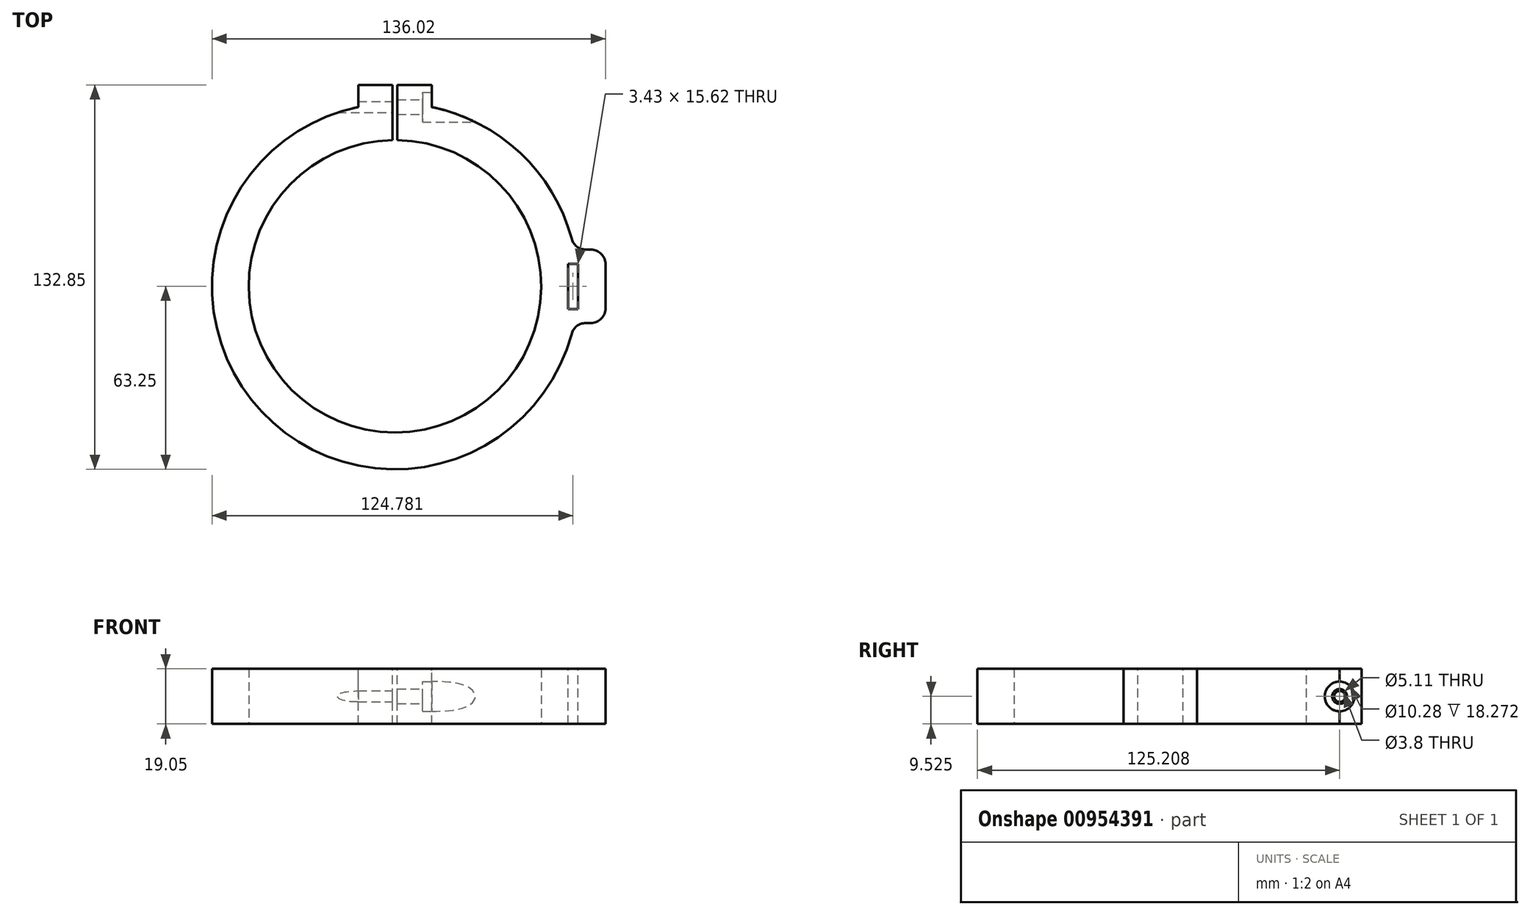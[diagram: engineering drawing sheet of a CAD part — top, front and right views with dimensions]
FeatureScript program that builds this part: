
annotation { "Feature Type Name" : "Feature", "Feature Type Description" : "" }
export const myFeature = defineFeature(function(context is Context, id is Id, definition is map)
    precondition{}
    {
        {
            var Q0;
            Q0=qCreatedBy(makeId("Top.planeOp"),FACE);
            var sketch = newSketch(context, id + "F0", { "sketchPlane" : qUnion([Q0])});
            skCircle(sketch, "E0", {"center": v(0, 0) * mm, "radius": 50.55 * mm});
            skCircle(sketch, "E1", {"center": v(0, 0) * mm, "radius": 63.25 * mm});
            skSolve(sketch);
        }
        {
            var Q0;
            Q0=makeQuery(id+"F0.imprint","IMPRINT",FACE,{"disambiguationData":[TD([[makeQuery(id+"F0.imprint","IMPRINT",EDGE,{"derivedFrom":sQuery(id+"F0.wireOp",EDGE,"E0")}),-1.0]])]});
            extrude(context, id + "F1", {"entities" : qUnion([Q0]), "depth" : 19.05 * mm, "offsetDistance" : 25.4 * mm});
        }
        {
            var Q0;
            Q0=makeQuery(id+"F1.opExtrude","CAP_FACE",FACE,{"disambiguationData":[OSD([sQuery(id+"F0.wireOp",EDGE,"E0"),sQuery(id+"F0.wireOp",EDGE,"E1")])],"isStart":false});
            var sketch = newSketch(context, id + "F2", { "sketchPlane" : qUnion([Q0])});
            skLineSegment(sketch, "E2.bottom", {"start": v(-12.7, 69.6) * mm, "end": v(12.7, 69.6) * mm});
            skLineSegment(sketch, "E2.top", {"start": v(-12.7, 50.55) * mm, "end": v(12.7, 50.55) * mm});
            skLineSegment(sketch, "E2.left", {"start": v(-12.7, 69.6) * mm, "end": v(-12.7, 50.55) * mm});
            skLineSegment(sketch, "E2.right", {"start": v(12.7, 69.6) * mm, "end": v(12.7, 50.55) * mm});
            skSolve(sketch);
        }
        {
            var Q0;
            {var subQ0=sQuery(id+"F2.wireOp",EDGE,"E2.bottom");Q0=makeQuery(id+"F2.imprint","IMPRINT",FACE,{"disambiguationData":[TD([[makeQuery(id+"F2.imprint","IMPRINT",EDGE,{"derivedFrom":subQ0}),-1.0]])]});}
            extrude(context, id + "F3", {"entities" : qUnion([Q0]), "operationType" : NewBodyOperationType.ADD, "oppositeDirection" : true, "depth" : 19.05 * mm, "offsetDistance" : 25.4 * mm});
        }
        {
            var Q0;
            {var subQ0=sQuery(id+"F0.wireOp",EDGE,"E1");Q0=makeQuery(id+"F3.boolean.opBoolean","MERGE",FACE,{"derivedFrom":[makeQuery(id+"F1.opExtrude","CAP_FACE",FACE,{"disambiguationData":[OSD([sQuery(id+"F0.wireOp",EDGE,"E0"),subQ0])],"isStart":false}),makeQuery(id+"F3.opExtrude","CAP_FACE",FACE,{"disambiguationData":[OSD([subQ0,sQuery(id+"F2.wireOp",EDGE,"E2.bottom"),sQuery(id+"F2.wireOp",EDGE,"E2.left"),sQuery(id+"F2.wireOp",EDGE,"E2.right")])],"isStart":true})]});}
            var sketch = newSketch(context, id + "F4", { "sketchPlane" : qUnion([Q0])});
            skLineSegment(sketch, "E3.bottom", {"start": v(-0.8, 69.6) * mm, "end": v(0.8, 69.6) * mm});
            skLineSegment(sketch, "E3.top", {"start": v(-0.8, 50.54) * mm, "end": v(0.8, 50.54) * mm});
            skLineSegment(sketch, "E3.left", {"start": v(-0.8, 69.6) * mm, "end": v(-0.8, 50.54) * mm});
            skLineSegment(sketch, "E3.right", {"start": v(0.8, 69.6) * mm, "end": v(0.8, 50.54) * mm});
            skSolve(sketch);
        }
        {
            var Q0;
            Q0 = qSketchRegion(id + "F4", true);
            extrude(context, id + "F5", {"entities" : qUnion([Q0]), "operationType" : NewBodyOperationType.REMOVE, "endBound" : BoundingType.THROUGH_ALL, "oppositeDirection" : true, "depth" : 25.4 * mm, "offsetDistance" : 25.4 * mm});
        }
        {
            var Q0;
            Q0=makeQuery(id+"F3.opExtrude","SWEPT_FACE",FACE,{"disambiguationData":[OSD([sQuery(id+"F2.wireOp",EDGE,"E2.right")])]});
            var sketch = newSketch(context, id + "F6", { "sketchPlane" : qUnion([Q0])});
            skCircle(sketch, "E4", {"center": v(61.96, 9.52) * mm, "radius": 2.55 * mm});
            skSolve(sketch);
        }
        {
            var Q0;
            Q0 = qSketchRegion(id + "F6", true);
            var Q1;
            Q1=makeQuery(id+"F5.boolean.opBoolean","COPY",FACE,{"derivedFrom":makeQuery(id+"F5.opExtrude","SWEPT_FACE",FACE,{"disambiguationData":[OSD([sQuery(id+"F4.wireOp",EDGE,"E3.right")])]})});
            extrude(context, id + "F7", {"entities" : qUnion([Q0]), "operationType" : NewBodyOperationType.REMOVE, "endBound" : BoundingType.UP_TO_SURFACE, "oppositeDirection" : true, "depth" : 25.4 * mm, "endBoundEntityFace" : qUnion([Q1]), "offsetDistance" : 25.4 * mm});
        }
        {
            var Q0;
            Q0=makeQuery(id+"F3.opExtrude","SWEPT_FACE",FACE,{"disambiguationData":[OSD([sQuery(id+"F2.wireOp",EDGE,"E2.right")])]});
            var sketch = newSketch(context, id + "F8", { "sketchPlane" : qUnion([Q0])});
            skCircle(sketch, "E5", {"center": v(61.96, 9.52) * mm, "radius": 5.14 * mm});
            skSolve(sketch);
        }
        {
            var Q0;
            Q0 = qSketchRegion(id + "F8", true);
            extrude(context, id + "F9", {"entities" : qUnion([Q0]), "operationType" : NewBodyOperationType.REMOVE, "oppositeDirection" : true, "depth" : 3.17 * mm, "offsetDistance" : 25.4 * mm, "hasSecondDirection" : true, "secondDirectionBound" : SecondDirectionBoundingType.THROUGH_ALL, "secondDirectionOppositeDirection" : false, "secondDirectionDepth" : 25.4 * mm});
        }
        {
            var Q0;
            Q0=makeQuery(id+"F5.boolean.opBoolean","COPY",FACE,{"derivedFrom":makeQuery(id+"F5.opExtrude","SWEPT_FACE",FACE,{"disambiguationData":[OSD([sQuery(id+"F4.wireOp",EDGE,"E3.left")])]})});
            var sketch = newSketch(context, id + "F10", { "sketchPlane" : qUnion([Q0])});
            skPoint(sketch, "E6", {"position": v(61.96, 9.52) * mm});
            skSolve(sketch);
        }
        {
            var Q0;
            Q0=sQuery(id+"F10.wireOp",VERTEX,"E6");
            var Q1;
            Q1=makeQuery(id+"F1.opExtrude","SWEPT_BODY",BODY,{"disambiguationData":[OSD([sQuery(id+"F0.wireOp",EDGE,"E0"),sQuery(id+"F0.wireOp",EDGE,"E1")])]});
            hole(context, id + "F11", {"style" : HoleStyle.SIMPLE, "endStyle" : HoleEndStyle.THROUGH, "standardTappedOrClearance" : lookupTablePath({ "standard" : "ANSI", "engagement" : "75%", "pitch" : "24 tpi", "size" : "#10", "type" : "Tapped" }), "standardBlindInLast" : lookupTablePath({ "standard" : "ANSI", "fit" : "Normal", "engagement" : "75%", "pitch" : "24 tpi", "size" : "#10", "type" : "Clearance & tapped" }), "holeDiameter" : 3.8 * mm, "majorDiameter" : 4.83 * mm, "showTappedDepth" : true, "isTappedThrough" : true, "tappedDepth" : 25.43 * mm, "tapClearance" : 3, "locations" : qUnion([Q0]), "scope" : qUnion([Q1])});
        }
        {
            var Q0;
            {var subQ0=sQuery(id+"F0.wireOp",EDGE,"E1");Q0=makeQuery(id+"F3.boolean.opBoolean","MERGE",FACE,{"derivedFrom":[makeQuery(id+"F1.opExtrude","CAP_FACE",FACE,{"disambiguationData":[OSD([sQuery(id+"F0.wireOp",EDGE,"E0"),subQ0])],"isStart":false}),makeQuery(id+"F3.opExtrude","CAP_FACE",FACE,{"disambiguationData":[OSD([subQ0,sQuery(id+"F2.wireOp",EDGE,"E2.bottom"),sQuery(id+"F2.wireOp",EDGE,"E2.left"),sQuery(id+"F2.wireOp",EDGE,"E2.right")])],"isStart":true})]});}
            var sketch = newSketch(context, id + "F12", { "sketchPlane" : qUnion([Q0])});
            skLineSegment(sketch, "E7.bottom", {"start": v(50.55, 12.7) * mm, "end": v(72.77, 12.7) * mm});
            skLineSegment(sketch, "E7.top", {"start": v(50.55, -12.7) * mm, "end": v(72.77, -12.7) * mm});
            skLineSegment(sketch, "E7.left", {"start": v(50.55, 12.7) * mm, "end": v(50.55, -12.7) * mm});
            skLineSegment(sketch, "E7.right", {"start": v(72.77, 12.7) * mm, "end": v(72.77, -12.7) * mm});
            skSolve(sketch);
        }
        {
            var Q0;
            Q0 = qSketchRegion(id + "F12", true);
            extrude(context, id + "F13", {"entities" : qUnion([Q0]), "operationType" : NewBodyOperationType.ADD, "oppositeDirection" : true, "depth" : 19.05 * mm, "offsetDistance" : 25.4 * mm});
        }
        {
            var Q0;
            {var subQ0=sQuery(id+"F0.wireOp",EDGE,"E1");Q0=makeQuery(id+"F13.boolean.opBoolean","MERGE",FACE,{"derivedFrom":[makeQuery(id+"F3.boolean.opBoolean","MERGE",FACE,{"derivedFrom":[makeQuery(id+"F1.opExtrude","CAP_FACE",FACE,{"disambiguationData":[OSD([sQuery(id+"F0.wireOp",EDGE,"E0"),subQ0])],"isStart":false}),makeQuery(id+"F3.opExtrude","CAP_FACE",FACE,{"disambiguationData":[OSD([subQ0,sQuery(id+"F2.wireOp",EDGE,"E2.bottom"),sQuery(id+"F2.wireOp",EDGE,"E2.left"),sQuery(id+"F2.wireOp",EDGE,"E2.right")])],"isStart":true})]}),makeQuery(id+"F13.opExtrude","CAP_FACE",FACE,{"disambiguationData":[OSD([sQuery(id+"F12.wireOp",EDGE,"E7.bottom"),sQuery(id+"F12.wireOp",EDGE,"E7.top"),sQuery(id+"F12.wireOp",EDGE,"E7.left"),sQuery(id+"F12.wireOp",EDGE,"E7.right")])],"isStart":true})]});}
            var sketch = newSketch(context, id + "F14", { "sketchPlane" : qUnion([Q0])});
            skLineSegment(sketch, "E8.bottom", {"start": v(59.82, 7.81) * mm, "end": v(63.25, 7.81) * mm});
            skLineSegment(sketch, "E8.top", {"start": v(59.82, -7.81) * mm, "end": v(63.25, -7.81) * mm});
            skLineSegment(sketch, "E8.left", {"start": v(59.82, 7.81) * mm, "end": v(59.82, -7.81) * mm});
            skLineSegment(sketch, "E8.right", {"start": v(63.25, 7.81) * mm, "end": v(63.25, -7.81) * mm});
            skSolve(sketch);
        }
        {
            var Q0;
            Q0=makeQuery(id+"F14.imprint","IMPRINT",FACE,{"disambiguationData":[TD([[makeQuery(id+"F14.imprint","IMPRINT",EDGE,{"derivedFrom":sQuery(id+"F14.wireOp",EDGE,"E8.bottom")}),-1.0]])]});
            extrude(context, id + "F15", {"entities" : qUnion([Q0]), "operationType" : NewBodyOperationType.REMOVE, "endBound" : BoundingType.THROUGH_ALL, "oppositeDirection" : true, "depth" : 25.4 * mm, "offsetDistance" : 25.4 * mm});
        }
        {
            var Q0;
            Q0=makeQuery(id+"F13.boolean.opBoolean","INTERSECT",EDGE,{"derivedFrom":[makeQuery(id+"F1.opExtrude","SWEPT_FACE",FACE,{"disambiguationData":[OSD([sQuery(id+"F0.wireOp",EDGE,"E1")])]}),makeQuery(id+"F13.opExtrude","SWEPT_FACE",FACE,{"disambiguationData":[OSD([sQuery(id+"F12.wireOp",EDGE,"E7.top")])]})]});
            var Q1;
            Q1=makeQuery(id+"F13.opExtrude","SWEPT_EDGE",EDGE,{"disambiguationData":[OSD([sQuery(id+"F12.wireOp",EDGE,"E7.top"),sQuery(id+"F12.wireOp",EDGE,"E7.right")])]});
            var Q2;
            Q2=makeQuery(id+"F13.opExtrude","SWEPT_EDGE",EDGE,{"disambiguationData":[OSD([sQuery(id+"F12.wireOp",EDGE,"E7.bottom"),sQuery(id+"F12.wireOp",EDGE,"E7.right")])]});
            var Q3;
            Q3=makeQuery(id+"F13.boolean.opBoolean","INTERSECT",EDGE,{"derivedFrom":[makeQuery(id+"F1.opExtrude","SWEPT_FACE",FACE,{"disambiguationData":[OSD([sQuery(id+"F0.wireOp",EDGE,"E1")])]}),makeQuery(id+"F13.opExtrude","SWEPT_FACE",FACE,{"disambiguationData":[OSD([sQuery(id+"F12.wireOp",EDGE,"E7.bottom")])]})]});
            var Q4;
            {var subQ0=sQuery(id+"F2.wireOp",EDGE,"E2.right");var subQ1=sQuery(id+"F0.wireOp",EDGE,"E1");var subQ2=makeQuery(id+"F1.opExtrude","SWEPT_FACE",FACE,{"disambiguationData":[OSD([subQ1])]});var subQ3=makeQuery(id+"F3.opExtrude","SWEPT_FACE",FACE,{"disambiguationData":[OSD([subQ0])]});Q4=makeQuery(id+"F7.boolean.opBoolean","SPLIT",EDGE,{"disambiguationData":[topologyDisambiguationEdgeConnected([subQ2,subQ3]),TD([makeQuery(id+"F1.opExtrude","CAP_FACE",FACE,{"disambiguationData":[OSD([sQuery(id+"F0.wireOp",EDGE,"E0"),subQ1])],"isStart":false})])],"derivedFrom":makeQuery(id+"F3.opExtrude","SWEPT_EDGE",EDGE,{"disambiguationData":[OSD([subQ1,subQ0])]})});}
            var Q5;
            {var subQ0=sQuery(id+"F2.wireOp",EDGE,"E2.right");var subQ1=makeQuery(id+"F3.opExtrude","SWEPT_FACE",FACE,{"disambiguationData":[OSD([subQ0])]});var subQ2=sQuery(id+"F0.wireOp",EDGE,"E1");var subQ3=makeQuery(id+"F1.opExtrude","SWEPT_FACE",FACE,{"disambiguationData":[OSD([subQ2])]});Q5=makeQuery(id+"F7.boolean.opBoolean","SPLIT",EDGE,{"disambiguationData":[topologyDisambiguationEdgeConnected([subQ3,subQ1]),TD([makeQuery(id+"F1.opExtrude","CAP_FACE",FACE,{"disambiguationData":[OSD([sQuery(id+"F0.wireOp",EDGE,"E0"),subQ2])],"isStart":true})])],"derivedFrom":makeQuery(id+"F3.opExtrude","SWEPT_EDGE",EDGE,{"disambiguationData":[OSD([subQ2,subQ0])]})});}
            var Q6;
            {var subQ0=sQuery(id+"F2.wireOp",EDGE,"E2.left");var subQ1=sQuery(id+"F0.wireOp",EDGE,"E1");Q6=makeQuery(id+"F11.hole-0.boolean.opBoolean","SPLIT",EDGE,{"disambiguationData":[TD([makeQuery(id+"F1.opExtrude","CAP_FACE",FACE,{"disambiguationData":[OSD([sQuery(id+"F0.wireOp",EDGE,"E0"),subQ1])],"isStart":false})])],"derivedFrom":makeQuery(id+"F3.opExtrude","SWEPT_EDGE",EDGE,{"disambiguationData":[OSD([subQ1,subQ0])]})});}
            var Q7;
            {var subQ0=sQuery(id+"F2.wireOp",EDGE,"E2.left");var subQ1=sQuery(id+"F0.wireOp",EDGE,"E1");Q7=makeQuery(id+"F11.hole-0.boolean.opBoolean","SPLIT",EDGE,{"disambiguationData":[TD([makeQuery(id+"F1.opExtrude","CAP_FACE",FACE,{"disambiguationData":[OSD([sQuery(id+"F0.wireOp",EDGE,"E0"),subQ1])],"isStart":true})])],"derivedFrom":makeQuery(id+"F3.opExtrude","SWEPT_EDGE",EDGE,{"disambiguationData":[OSD([subQ1,subQ0])]})});}
            fillet(context, id + "F16", {"entities" : qUnion([Q0, Q1, Q2, Q3, Q4, Q5, Q6, Q7]), "radius" : 5.08 * mm, "tangentPropagation" : true, "allowEdgeOverflow" : false});
        }
    });
